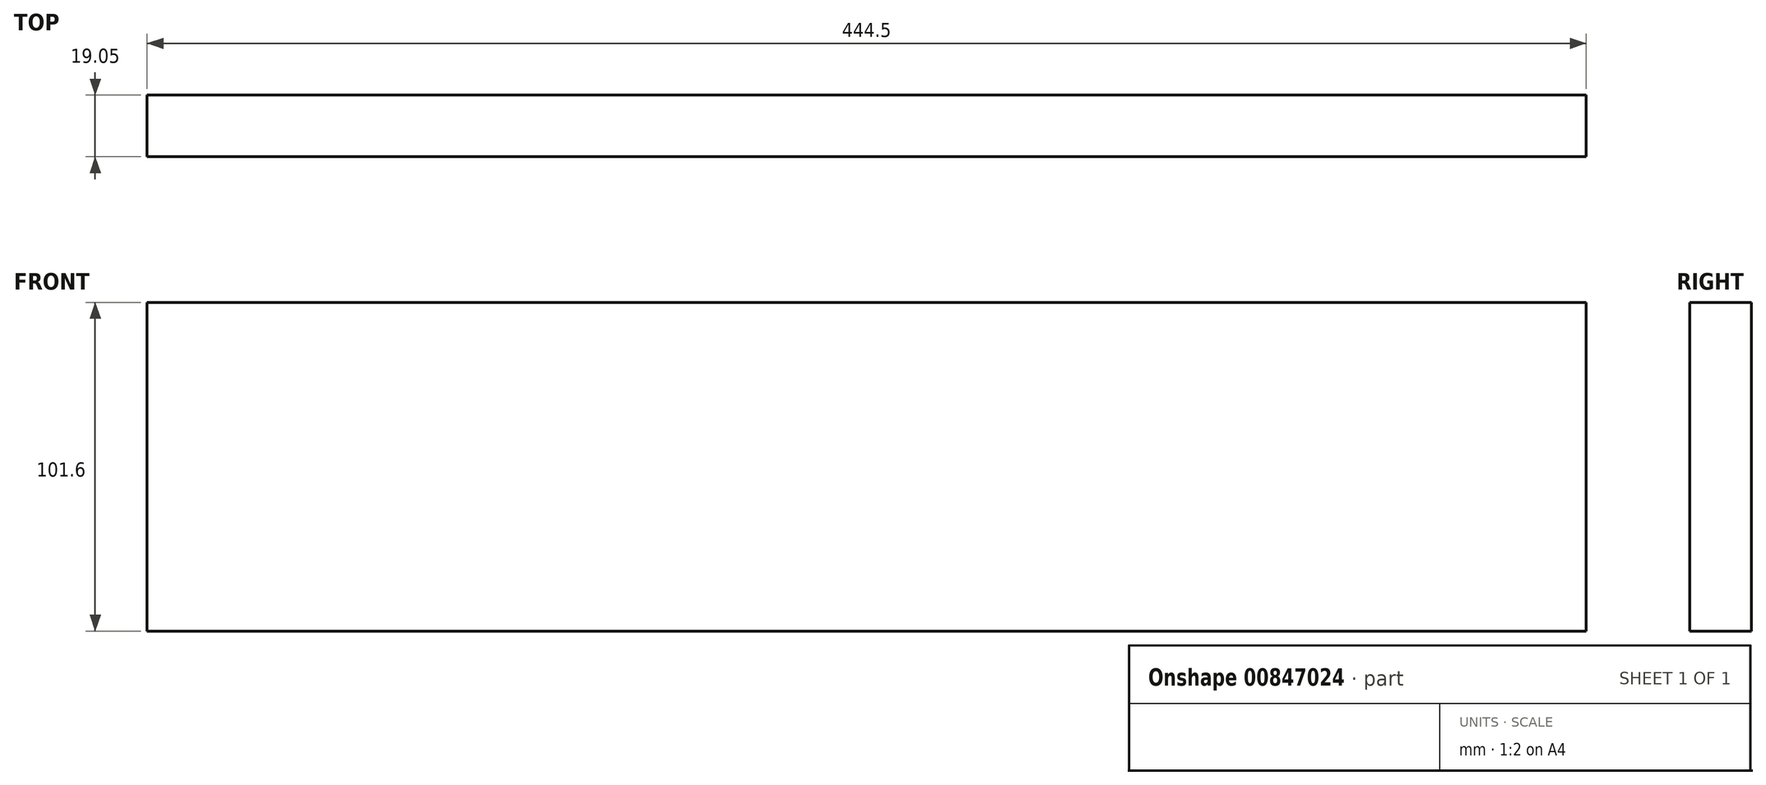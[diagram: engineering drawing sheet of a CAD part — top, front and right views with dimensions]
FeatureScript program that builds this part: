
annotation { "Feature Type Name" : "Feature", "Feature Type Description" : "" }
export const myFeature = defineFeature(function(context is Context, id is Id, definition is map)
    precondition{}
    {
        {
            var Q0;
            Q0=qCreatedBy(makeId("Front.planeOp"),FACE);
            var sketch = newSketch(context, id + "F0", { "sketchPlane" : qUnion([Q0])});
            skLineSegment(sketch, "E0.bottom", {"start": v(-163.34, -55.94) * mm, "end": v(281.16, -55.94) * mm});
            skLineSegment(sketch, "E0.top", {"start": v(-163.34, 45.66) * mm, "end": v(281.16, 45.66) * mm});
            skLineSegment(sketch, "E0.left", {"start": v(-163.34, -55.94) * mm, "end": v(-163.34, 45.66) * mm});
            skLineSegment(sketch, "E0.right", {"start": v(281.16, -55.94) * mm, "end": v(281.16, 45.66) * mm});
            skSolve(sketch);
        }
        {
            var Q0;
            Q0 = qSketchRegion(id + "F0", true);
            extrude(context, id + "F1", {"entities" : qUnion([Q0]), "depth" : 19.05 * mm, "offsetDistance" : 25.4 * mm});
        }
    });
